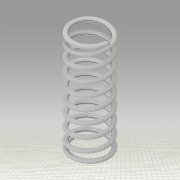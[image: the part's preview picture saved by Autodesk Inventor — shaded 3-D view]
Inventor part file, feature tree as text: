
AUTODESK INVENTOR PART (.ipt)
format: ipt  version: 2018 (Build 220112000, 112)  size: 439,808 bytes
history: native  units: in
note: dims shown in document units (in); Inventor stores cm internally (conversion verified against a paired STEP export)
features: helix x1, sketch x1
ambient origin geometry x8: Origin, YZ Plane, XZ Plane, XY Plane, X Axis, Y Axis, Z Axis, Center Point
bodies: Solid1 (feature_tree)
feature tree (2):
  helix  "Coil1"  [1 undecoded]
  sketch  "Sketch1"  dims[d1=0.147in d2=1.0in d3=0.75in d4=3.1496in d5=0.0in d6=90.0deg d7=180.0deg d8=90.0deg d9=180.0deg]
note: 1 required parameter value undecoded (feature->parameter linkage not recoverable at this tier; creation-order binding heuristic only, values carry confidence <= 0.55)
